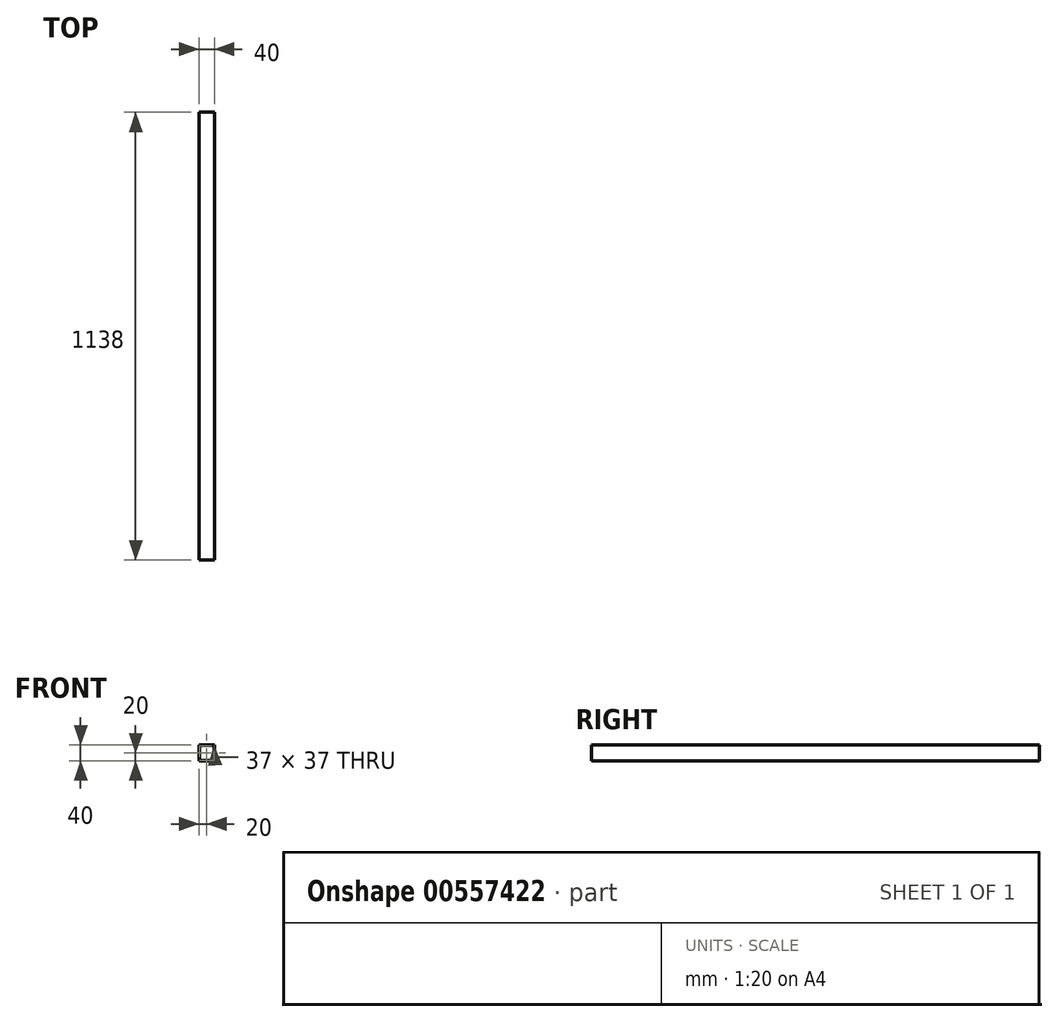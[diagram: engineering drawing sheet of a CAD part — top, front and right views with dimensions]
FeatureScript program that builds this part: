
annotation { "Feature Type Name" : "Feature", "Feature Type Description" : "" }
export const myFeature = defineFeature(function(context is Context, id is Id, definition is map)
    precondition{}
    {
        {
            var Q0;
            Q0=qCreatedBy(makeId("Front.planeOp"),FACE);
            var sketch = newSketch(context, id + "F0", { "sketchPlane" : qUnion([Q0])});
            skLineSegment(sketch, "E0.bottom", {"start": v(20, 20) * mm, "end": v(-20, 20) * mm});
            skLineSegment(sketch, "E0.top", {"start": v(20, -20) * mm, "end": v(-20, -20) * mm});
            skLineSegment(sketch, "E0.left", {"start": v(20, 20) * mm, "end": v(20, -20) * mm});
            skLineSegment(sketch, "E0.right", {"start": v(-20, 20) * mm, "end": v(-20, -20) * mm});
            skPoint(sketch, "E0.middle", {"position": v(0, 0) * mm});
            skLineSegment(sketch, "E1.0", {"start": v(-18.5, 18.5) * mm, "end": v(-18.5, -18.5) * mm});
            skLineSegment(sketch, "E1.1", {"start": v(18.5, 18.5) * mm, "end": v(-18.5, 18.5) * mm});
            skLineSegment(sketch, "E1.2", {"start": v(18.5, 18.5) * mm, "end": v(18.5, -18.5) * mm});
            skLineSegment(sketch, "E1.3", {"start": v(18.5, -18.5) * mm, "end": v(-18.5, -18.5) * mm});
            skSolve(sketch);
        }
        {
            var Q0;
            Q0=makeQuery(id+"F0.imprint","IMPRINT",FACE,{"disambiguationData":[TD([[makeQuery(id+"F0.imprint","IMPRINT",EDGE,{"derivedFrom":sQuery(id+"F0.wireOp",EDGE,"E0.bottom")}),1.0]])]});
            extrude(context, id + "F1", {"entities" : qUnion([Q0]), "endBound" : BoundingType.SYMMETRIC, "depth" : 1138 * mm, "offsetDistance" : 25 * mm});
        }
    });
